# Revit family: Скамейка стальная «Адонис»  Арт 14146
name_source: partatom
category: Антураж
revit_build: Autodesk Revit 2018 (Build: 20180423_1000(x64)
units: mm (PartAtom-declared; Revit-internal decimal feet)

## family parameters
Всегда вертикально = Да
Источник визуального образа = Геометрия семейства
На основе рабочей плоскости = Нет
Общий = Нет
При загрузке вырезать с полостями = Нет
Точка расчета площади = Нет

## types (2) — shared parameters
URL = https://hobbyka.ru
Артикул товара = Арт. 14146
Высота = 784 мм
Группа модели = Скамейки
Длина = 2000 мм
Изготовитель = ООО «Хоббика»
Материал изделия = Сталь, дерево
Цвет лавки = Дерево
Цвет опоры = Сталь

## per-type parameters (varying)
| type | Двухсторонняя | Изображение типоразмера | Односторонняя | Описание | Ширина |
| Односторонняя | Нет | Скамейка стальная «Адонис»  Арт 14146 Односторонняя.jpg | Да | Скамейка стальная «Адонис». Версия 2,0 м. Односторонняя | 580 мм |
| Двухсторонняя | Да | Скамейка стальная «Адонис»  Арт 14146 Двухсторонняя.jpg | Нет | Скамейка стальная «Адонис». Версия 2,0 м. Двухсторонняя | 659 мм |
